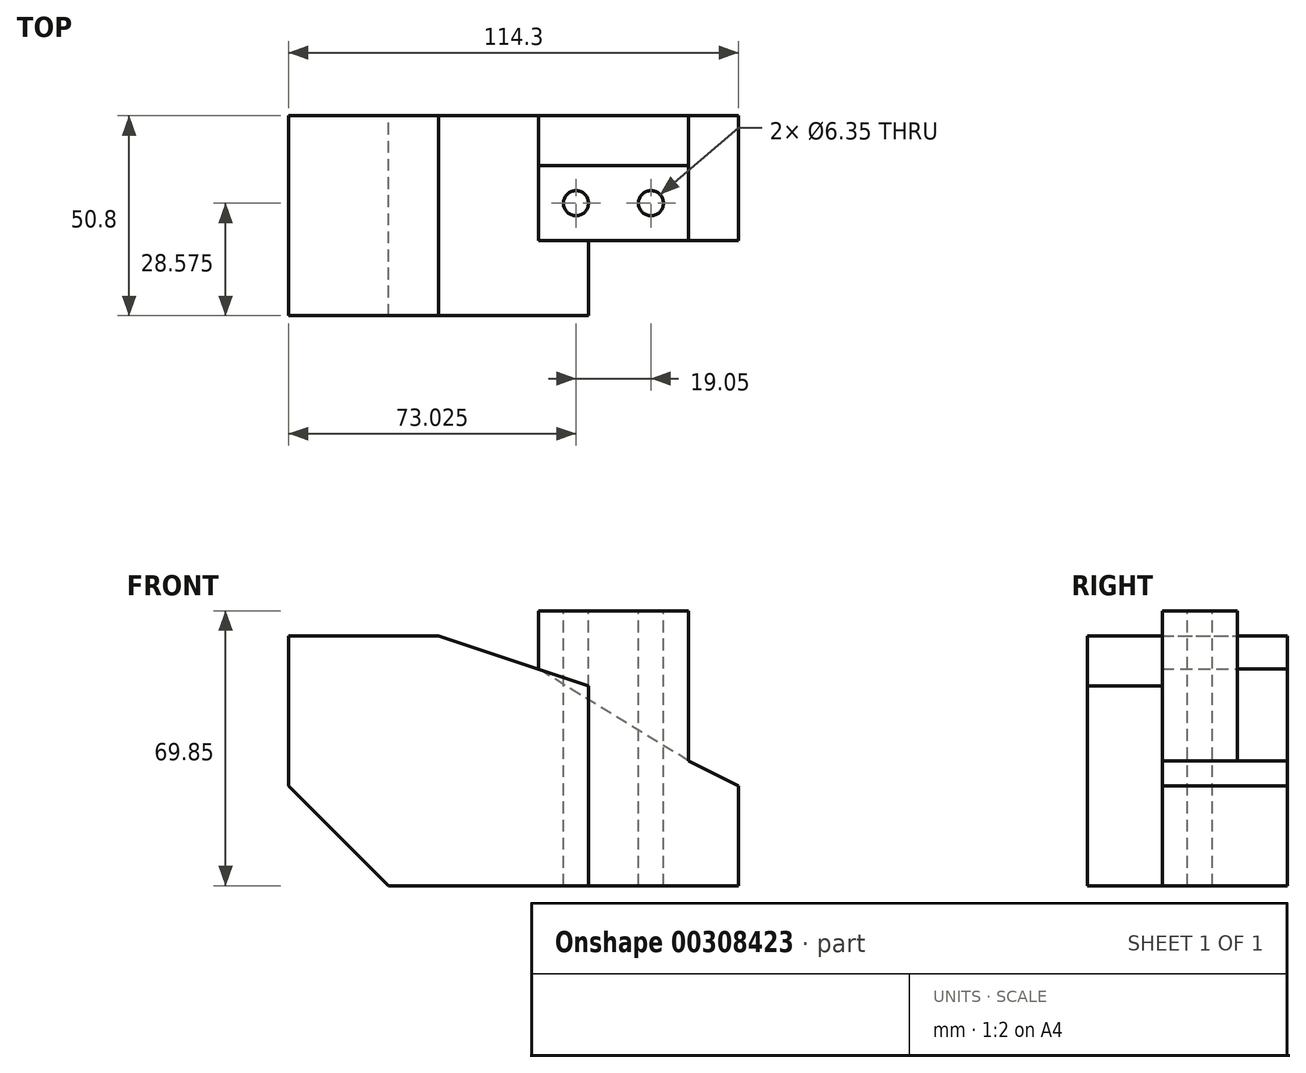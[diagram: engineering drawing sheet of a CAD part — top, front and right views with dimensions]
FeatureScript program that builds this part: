
annotation { "Feature Type Name" : "Feature", "Feature Type Description" : "" }
export const myFeature = defineFeature(function(context is Context, id is Id, definition is map)
    precondition{}
    {
        {
            var Q0;
            Q0=qCreatedBy(makeId("Front.planeOp"),FACE);
            var sketch = newSketch(context, id + "F0", { "sketchPlane" : qUnion([Q0])});
            skLineSegment(sketch, "E0", {"start": v(0, 0) * mm, "end": v(0, 25.4) * mm});
            skLineSegment(sketch, "E1", {"start": v(0, 0) * mm, "end": v(25.4, 0) * mm});
            skLineSegment(sketch, "E2", {"start": v(25.4, 0) * mm, "end": v(0, 25.4) * mm});
            skLineSegment(sketch, "E3", {"start": v(0, 25.4) * mm, "end": v(0, 63.5) * mm});
            skLineSegment(sketch, "E4", {"start": v(0, 63.5) * mm, "end": v(38.1, 63.5) * mm});
            skLineSegment(sketch, "E5", {"start": v(25.4, 0) * mm, "end": v(76.2, 0) * mm});
            skLineSegment(sketch, "E6", {"start": v(76.2, 0) * mm, "end": v(76.2, 50.8) * mm});
            skLineSegment(sketch, "E7", {"start": v(76.2, 50.8) * mm, "end": v(38.1, 63.5) * mm});
            skLineSegment(sketch, "E8", {"start": v(76.2, 0) * mm, "end": v(114.3, 0) * mm});
            skLineSegment(sketch, "E9", {"start": v(114.3, 0) * mm, "end": v(114.3, 25.4) * mm});
            skLineSegment(sketch, "E10", {"start": v(76.2, 50.8) * mm, "end": v(76.2, 69.85) * mm});
            skLineSegment(sketch, "E11", {"start": v(76.2, 69.85) * mm, "end": v(63.5, 69.85) * mm});
            skLineSegment(sketch, "E12", {"start": v(63.5, 69.85) * mm, "end": v(63.5, 55.03) * mm});
            skLineSegment(sketch, "E13", {"start": v(76.2, 69.85) * mm, "end": v(101.6, 69.85) * mm});
            skLineSegment(sketch, "E14", {"start": v(101.6, 69.85) * mm, "end": v(101.6, 31.75) * mm});
            skLineSegment(sketch, "E15", {"start": v(101.6, 31.75) * mm, "end": v(114.3, 25.4) * mm});
            skSolve(sketch);
        }
        {
            var Q0;
            Q0=makeQuery(id+"F0.imprint","IMPRINT",FACE,{"disambiguationData":[TD([[makeQuery(id+"F0.imprint","IMPRINT",EDGE,{"derivedFrom":sQuery(id+"F0.wireOp",EDGE,"E2")}),-1.0]])]});
            var Q1;
            Q1=makeQuery(id+"F0.imprint","IMPRINT",FACE,{"disambiguationData":[TD([[makeQuery(id+"F0.imprint","IMPRINT",EDGE,{"derivedFrom":sQuery(id+"F0.wireOp",EDGE,"E6")}),-1.0]])]});
            var Q2;
            {var subQ0=sQuery(id+"F0.wireOp",EDGE,"E10");Q2=makeQuery(id+"F0.imprint","IMPRINT",FACE,{"disambiguationData":[TD([[makeQuery(id+"F0.imprint","IMPRINT",EDGE,{"derivedFrom":subQ0}),1.0]])]});}
            extrude(context, id + "F1", {"entities" : qUnion([Q0, Q1, Q2]), "endBound" : BoundingType.SYMMETRIC, "depth" : 50.8 * mm});
        }
        {
            var Q0;
            Q0=makeQuery(id+"F1.opExtrude","CAP_FACE",FACE,{"disambiguationData":[OSD([sQuery(id+"F0.wireOp",EDGE,"E2"),sQuery(id+"F0.wireOp",EDGE,"E3"),sQuery(id+"F0.wireOp",EDGE,"E4"),sQuery(id+"F0.wireOp",EDGE,"E5"),sQuery(id+"F0.wireOp",EDGE,"E7"),sQuery(id+"F0.wireOp",EDGE,"E8"),sQuery(id+"F0.wireOp",EDGE,"E9"),sQuery(id+"F0.wireOp",EDGE,"E11"),sQuery(id+"F0.wireOp",EDGE,"E12"),sQuery(id+"F0.wireOp",EDGE,"E13"),sQuery(id+"F0.wireOp",EDGE,"E14"),sQuery(id+"F0.wireOp",EDGE,"E15")])],"isStart":false});
            var sketch = newSketch(context, id + "F2", { "sketchPlane" : qUnion([Q0])});
            skLineSegment(sketch, "E16", {"start": v(114.3, 0) * mm, "end": v(76.2, 0) * mm});
            skLineSegment(sketch, "E17", {"start": v(76.2, 0) * mm, "end": v(76.2, 50.8) * mm});
            skLineSegment(sketch, "E18", {"start": v(76.2, 50.8) * mm, "end": v(63.5, 55.03) * mm});
            skLineSegment(sketch, "E19", {"start": v(63.5, 55.03) * mm, "end": v(63.5, 69.85) * mm});
            skLineSegment(sketch, "E20", {"start": v(63.5, 69.85) * mm, "end": v(101.6, 69.85) * mm});
            skLineSegment(sketch, "E21", {"start": v(101.6, 69.85) * mm, "end": v(101.6, 31.75) * mm});
            skLineSegment(sketch, "E22", {"start": v(101.6, 31.75) * mm, "end": v(114.3, 25.4) * mm});
            skLineSegment(sketch, "E23", {"start": v(114.3, 25.4) * mm, "end": v(114.3, 0) * mm});
            skSolve(sketch);
        }
        {
            var Q0;
            Q0 = qSketchRegion(id + "F2", true);
            extrude(context, id + "F3", {"entities" : qUnion([Q0]), "operationType" : NewBodyOperationType.REMOVE, "oppositeDirection" : true, "depth" : 19.05 * mm});
        }
        {
            var Q0;
            Q0=makeQuery(id+"F1.opExtrude","CAP_FACE",FACE,{"disambiguationData":[OSD([sQuery(id+"F0.wireOp",EDGE,"E2"),sQuery(id+"F0.wireOp",EDGE,"E3"),sQuery(id+"F0.wireOp",EDGE,"E4"),sQuery(id+"F0.wireOp",EDGE,"E5"),sQuery(id+"F0.wireOp",EDGE,"E7"),sQuery(id+"F0.wireOp",EDGE,"E8"),sQuery(id+"F0.wireOp",EDGE,"E9"),sQuery(id+"F0.wireOp",EDGE,"E11"),sQuery(id+"F0.wireOp",EDGE,"E12"),sQuery(id+"F0.wireOp",EDGE,"E13"),sQuery(id+"F0.wireOp",EDGE,"E14"),sQuery(id+"F0.wireOp",EDGE,"E15")])],"isStart":true});
            var sketch = newSketch(context, id + "F4", { "sketchPlane" : qUnion([Q0])});
            skLineSegment(sketch, "E24", {"start": v(-114.3, 25.4) * mm, "end": v(-101.6, 31.75) * mm});
            skLineSegment(sketch, "E25", {"start": v(-101.6, 31.75) * mm, "end": v(-63.5, 55.03) * mm});
            skLineSegment(sketch, "E26", {"start": v(-63.5, 55.03) * mm, "end": v(-63.5, 69.85) * mm});
            skLineSegment(sketch, "E27", {"start": v(-63.5, 69.85) * mm, "end": v(-101.6, 69.85) * mm});
            skLineSegment(sketch, "E28", {"start": v(-101.6, 69.85) * mm, "end": v(-101.6, 31.75) * mm});
            skSolve(sketch);
        }
        {
            var Q0;
            Q0=makeQuery(id+"F4.imprint","IMPRINT",FACE,{"disambiguationData":[TD([[makeQuery(id+"F4.imprint","IMPRINT",EDGE,{"derivedFrom":sQuery(id+"F4.wireOp",EDGE,"E25")}),1.0]])]});
            extrude(context, id + "F5", {"entities" : qUnion([Q0]), "operationType" : NewBodyOperationType.REMOVE, "oppositeDirection" : true, "depth" : 12.7 * mm});
        }
        {
            var Q0;
            Q0=makeQuery(id+"F1.opExtrude","SWEPT_FACE",FACE,{"disambiguationData":[OSD([sQuery(id+"F0.wireOp",EDGE,"E11"),sQuery(id+"F0.wireOp",EDGE,"E13")])]});
            var sketch = newSketch(context, id + "F6", { "sketchPlane" : qUnion([Q0])});
            skLineSegment(sketch, "E29", {"start": v(63.5, 3.17) * mm, "end": v(101.6, 3.17) * mm, "construction": true});
            skPoint(sketch, "E30", {"position": v(73.03, 3.17) * mm});
            skPoint(sketch, "E31", {"position": v(92.08, 3.17) * mm});
            skCircle(sketch, "E32", {"center": v(73.03, 3.17) * mm, "radius": 3.18 * mm});
            skCircle(sketch, "E33", {"center": v(92.08, 3.17) * mm, "radius": 3.18 * mm});
            skSolve(sketch);
        }
        {
            var Q0;
            Q0 = qSketchRegion(id + "F6", true);
            extrude(context, id + "F7", {"entities" : qUnion([Q0]), "operationType" : NewBodyOperationType.REMOVE, "endBound" : BoundingType.THROUGH_ALL, "oppositeDirection" : true, "depth" : 25.4 * mm});
        }
    });
